# Revit family: FU_Table_Sandler_Mesa 0114-Complete
name_source: partatom
category: Furniture
units: mm (PartAtom-declared; Revit-internal decimal feet)

## family parameters
Always vertical = Yes
Cut with Voids When Loaded = No
OmniClass Number = 23.40.20.00
OmniClass Title = General Furniture and Specialties
Render Appearance Source = Family Geometry
Room Calculation Point = No
Shared = No
Work Plane-Based = No

## types (10) — shared parameters
Depth = 465 mm  [stored 1.52559 ft]
Description = Steel table base at bar height. Steel central column, round base plate. Works with Mesa tabletops.
Height = 1030 mm  [stored 3.37927 ft]
Manufacturer = Sandler
Model = Mesa 0014
URL = https://www.sandlerseating.com
Width = 465 mm  [stored 1.52559 ft]
zero-valued in all types: Default Elevation

## per-type parameters (varying)
| type | Top Type |
| Mesa 0014 - HPL Rnd 60 | IC_TT_Rnd_HPL : HPL Rnd Top 60 |
| Mesa 0014 - HPL Rnd 70 | IC_TT_Rnd_HPL : HPL Rnd Top 70 |
| Mesa 0014 - HPL Rnd 80 | IC_TT_Rnd_HPL : HPL Rnd Top 80 |
| Mesa 0014 - Wood Rnd 60 | IC_TT_Rnd_Wood : Wood Rnd Top 60 |
| Mesa 0014 - Wood Rnd 70 | IC_TT_Rnd_Wood : Wood Rnd Top 70 |
| Mesa 0014 - Wood Rnd 80 | IC_TT_Rnd_Wood : Wood Rnd Top 80 |
| Mesa 0014 - HPL Sqr 60 | IC_TT_Sqr_HPL : HPL Sqr Top 60 |
| Mesa 0014 - HPL Sqr 70 | IC_TT_Sqr_HPL : HPL Sqr Top 70 |
| Mesa 0014 - Wood Sqr 60 | IC_TT_Sqr_Wood : Wood Sqr Top 60 |
| Mesa 0014 - Wood Sqr 70 | IC_TT_Sqr_Wood : Wood Sqr Top 70 |

note: [stored X ft] marks values corroborated as IEEE doubles in the binary element streams (Revit-internal decimal feet)

## geometry (parser evidence)
native form markers: Sweep x12
no freeform markers — native parametric forms only
